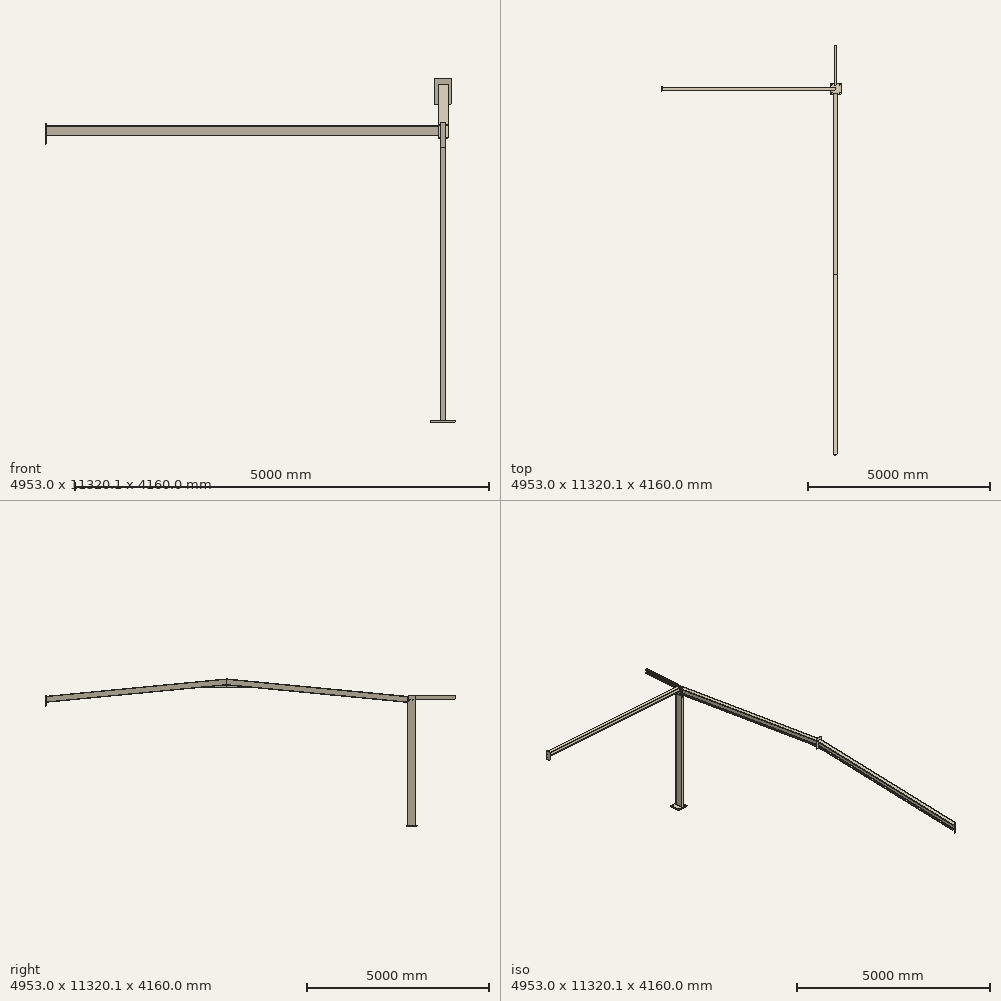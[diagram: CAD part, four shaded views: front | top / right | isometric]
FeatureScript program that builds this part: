
annotation { "Feature Type Name" : "Feature", "Feature Type Description" : "" }
export const myFeature = defineFeature(function(context is Context, id is Id, definition is map)
    precondition{}
    {
        {
            var Q0;
            Q0=qCreatedBy(makeId("Right.planeOp"),FACE);
            var sketch = newSketch(context, id + "F0", { "sketchPlane" : qUnion([Q0])});
            skLineSegment(sketch, "E0", {"start": v(-363, 0) * mm, "end": v(480.55, 0) * mm, "construction": true});
            skLineSegment(sketch, "E1", {"start": v(0, 0) * mm, "end": v(-4976.98, -479.23) * mm, "construction": true});
            skLineSegment(sketch, "E2", {"start": v(0, 0) * mm, "end": v(-23.08, 239.68) * mm, "construction": true});
            skLineSegment(sketch, "E3", {"start": v(0, 0) * mm, "end": v(4976.98, -479.23) * mm, "construction": true});
            skLineSegment(sketch, "E4", {"start": v(0, 0) * mm, "end": v(23.08, 239.68) * mm, "construction": true});
            skLineSegment(sketch, "E5.0", {"start": v(4976.98, -479.23) * mm, "end": v(5000.06, -239.54) * mm});
            skLineSegment(sketch, "E6.0", {"start": v(-4976.98, -479.23) * mm, "end": v(-5000.06, -239.54) * mm});
            skPoint(sketch, "E7.orphan", {"position": v(480.55, -46.27) * mm});
            skSolve(sketch);
        }
        {
            var Q0;
            Q0=sQuery(id+"F0.wireOp",EDGE,"E2");
            cPlane(context, id + "F1", {"entities" : qUnion([Q0]), "cplaneType" : CPlaneType.LINE_ANGLE, "offset" : 25 * mm, "angle" : 90 * degree, "width" : 150 * mm, "height" : 150 * mm});
        }
        {
            var Q0;
            Q0=sQuery(id+"F0.wireOp",EDGE,"E4");
            cPlane(context, id + "F2", {"entities" : qUnion([Q0]), "cplaneType" : CPlaneType.LINE_ANGLE, "offset" : 25 * mm, "angle" : 90 * degree, "width" : 150 * mm, "height" : 150 * mm});
        }
        {
            var Q0;
            Q0=qCreatedBy(makeId("Front.planeOp"),FACE);
            var sketch = newSketch(context, id + "F3", { "sketchPlane" : qUnion([Q0])});
            skLineSegment(sketch, "E8.bottom", {"start": v(100, -160) * mm, "end": v(-100, -160) * mm});
            skLineSegment(sketch, "E8.top", {"start": v(100, 160) * mm, "end": v(-100, 160) * mm});
            skLineSegment(sketch, "E8.left", {"start": v(100, -160) * mm, "end": v(100, 160) * mm});
            skLineSegment(sketch, "E8.right", {"start": v(-100, -160) * mm, "end": v(-100, 160) * mm});
            skPoint(sketch, "E8.middle", {"position": v(0, 0) * mm});
            skSolve(sketch);
        }
        {
            var Q0;
            Q0=qCreatedBy(id+"F1.planeOp",FACE);
            cPlane(context, id + "F4", {"entities" : qUnion([Q0]), "cplaneType" : CPlaneType.OFFSET, "offset" : 5000 * mm, "oppositeDirection" : true, "width" : 150 * mm, "height" : 150 * mm});
        }
        {
            var Q0;
            Q0=qCreatedBy(id+"F2.planeOp",FACE);
            cPlane(context, id + "F5", {"entities" : qUnion([Q0]), "cplaneType" : CPlaneType.OFFSET, "offset" : 5020 * mm, "width" : 150 * mm, "height" : 150 * mm});
        }
        {
            var Q0;
            Q0=qCreatedBy(id+"F5.planeOp",FACE);
            var sketch = newSketch(context, id + "F6", { "sketchPlane" : qUnion([Q0])});
            skLineSegment(sketch, "E9", {"start": v(60, 82.46) * mm, "end": v(-60, 82.46) * mm});
            skLineSegment(sketch, "E10", {"start": v(-60, 82.46) * mm, "end": v(-60, 72.46) * mm});
            skLineSegment(sketch, "E11", {"start": v(-60, 72.46) * mm, "end": v(-5, 72.46) * mm});
            skLineSegment(sketch, "E12", {"start": v(-5, 72.46) * mm, "end": v(-5, -72.46) * mm});
            skLineSegment(sketch, "E13", {"start": v(-5, -72.46) * mm, "end": v(-60, -72.46) * mm});
            skLineSegment(sketch, "E14", {"start": v(-60, -72.46) * mm, "end": v(-60, -82.46) * mm});
            skLineSegment(sketch, "E15", {"start": v(-60, -82.46) * mm, "end": v(60, -82.46) * mm});
            skLineSegment(sketch, "E16", {"start": v(60, -82.46) * mm, "end": v(60, -72.46) * mm});
            skLineSegment(sketch, "E17", {"start": v(60, -72.46) * mm, "end": v(5, -72.46) * mm});
            skLineSegment(sketch, "E18", {"start": v(5, -72.46) * mm, "end": v(5, 72.46) * mm});
            skLineSegment(sketch, "E19", {"start": v(5, 72.46) * mm, "end": v(60, 72.46) * mm});
            skLineSegment(sketch, "E20", {"start": v(60, 72.46) * mm, "end": v(60, 82.46) * mm});
            skPoint(sketch, "E21", {"position": v(-322.82, 17) * mm});
            skLineSegment(sketch, "E22", {"start": v(-5, 0) * mm, "end": v(5, 0) * mm, "construction": true});
            skPoint(sketch, "E23", {"position": v(0, 0) * mm});
            skSolve(sketch);
        }
        {
            var Q0;
            Q0=qSketchRegion(id+"F3",true);
            extrude(context, id + "F7", {"entities" : qUnion([Q0]), "depth" : 10 * mm});
        }
        {
            var Q0;
            Q0=qSketchRegion(id+"F6",true);
            extrude(context, id + "F8", {"entities" : qUnion([Q0]), "operationType" : NewBodyOperationType.ADD, "endBound" : BoundingType.UP_TO_NEXT, "oppositeDirection" : true, "depth" : 25 * mm});
        }
        {
            var Q0;
            Q0=qCreatedBy(id+"F4.planeOp",FACE);
            var sketch = newSketch(context, id + "F9", { "sketchPlane" : qUnion([Q0])});
            skLineSegment(sketch, "E24", {"start": v(60, 82.46) * mm, "end": v(-60, 82.46) * mm});
            skLineSegment(sketch, "E25", {"start": v(-60, 82.46) * mm, "end": v(-60, 72.46) * mm});
            skLineSegment(sketch, "E26", {"start": v(-60, 72.46) * mm, "end": v(-5, 72.46) * mm});
            skLineSegment(sketch, "E27", {"start": v(-5, 72.46) * mm, "end": v(-5, -72.46) * mm});
            skLineSegment(sketch, "E28", {"start": v(-5, -72.46) * mm, "end": v(-60, -72.46) * mm});
            skLineSegment(sketch, "E29", {"start": v(-60, -72.46) * mm, "end": v(-60, -82.46) * mm});
            skLineSegment(sketch, "E30", {"start": v(-60, -82.46) * mm, "end": v(60, -82.46) * mm});
            skLineSegment(sketch, "E31", {"start": v(60, -82.46) * mm, "end": v(60, -72.46) * mm});
            skLineSegment(sketch, "E32", {"start": v(60, -72.46) * mm, "end": v(5, -72.46) * mm});
            skLineSegment(sketch, "E33", {"start": v(5, -72.46) * mm, "end": v(5, 72.46) * mm});
            skLineSegment(sketch, "E34", {"start": v(5, 72.46) * mm, "end": v(60, 72.46) * mm});
            skLineSegment(sketch, "E35", {"start": v(60, 72.46) * mm, "end": v(60, 82.46) * mm});
            skPoint(sketch, "E36", {"position": v(-971.4, 551) * mm});
            skLineSegment(sketch, "E37", {"start": v(-5, 0) * mm, "end": v(5, 0) * mm, "construction": true});
            skPoint(sketch, "E38", {"position": v(0, 0) * mm});
            skSolve(sketch);
        }
        {
            var Q0;
            Q0=qSketchRegion(id+"F9",true);
            extrude(context, id + "F10", {"entities" : qUnion([Q0]), "operationType" : NewBodyOperationType.ADD, "endBound" : BoundingType.UP_TO_NEXT, "depth" : 25 * mm});
        }
        {
            var Q0;
            Q0=qCreatedBy(makeId("Top.planeOp"),FACE);
            cPlane(context, id + "F11", {"entities" : qUnion([Q0]), "cplaneType" : CPlaneType.OFFSET, "offset" : 4000 * mm, "oppositeDirection" : true, "width" : 150 * mm, "height" : 150 * mm});
        }
        {
            var Q0;
            Q0=qCreatedBy(id+"F11.planeOp",FACE);
            var sketch = newSketch(context, id + "F12", { "sketchPlane" : qUnion([Q0])});
            skLineSegment(sketch, "E39.bottom", {"start": v(150, 5276.98) * mm, "end": v(-150, 5276.98) * mm});
            skLineSegment(sketch, "E39.top", {"start": v(150, 4976.98) * mm, "end": v(-150, 4976.98) * mm});
            skLineSegment(sketch, "E39.left", {"start": v(150, 5276.98) * mm, "end": v(150, 4976.98) * mm});
            skLineSegment(sketch, "E39.right", {"start": v(-150, 5276.98) * mm, "end": v(-150, 4976.98) * mm});
            skLineSegment(sketch, "E40", {"start": v(150, 4976.98) * mm, "end": v(-150, 5276.98) * mm, "construction": true});
            skPoint(sketch, "E41", {"position": v(0, 4976.98) * mm});
            skSolve(sketch);
        }
        {
            var Q0;
            Q0=qSketchRegion(id+"F12",true);
            extrude(context, id + "F13", {"entities" : qUnion([Q0]), "depth" : 25 * mm});
        }
        {
            var Q0;
            Q0=makeQuery(id+"F13.opExtrude","CAP_FACE",FACE,{"disambiguationData":[OSD([sQuery(id+"F12.wireOp",EDGE,"E39.bottom"),sQuery(id+"F12.wireOp",EDGE,"E39.top"),sQuery(id+"F12.wireOp",EDGE,"E39.left"),sQuery(id+"F12.wireOp",EDGE,"E39.right")])],"isStart":false});
            var sketch = newSketch(context, id + "F14", { "sketchPlane" : qUnion([Q0])});
            skLineSegment(sketch, "E42", {"start": v(25.6, 5220.06) * mm, "end": v(-25.6, 5220.06) * mm});
            skLineSegment(sketch, "E43", {"start": v(-25.6, 5220.06) * mm, "end": v(-25.6, 5212.06) * mm});
            skLineSegment(sketch, "E44", {"start": v(-25.6, 5212.06) * mm, "end": v(-3, 5212.06) * mm});
            skLineSegment(sketch, "E45", {"start": v(-3, 5212.06) * mm, "end": v(-3, 5008.06) * mm});
            skLineSegment(sketch, "E46", {"start": v(-3, 5008.06) * mm, "end": v(-25.6, 5008.06) * mm});
            skLineSegment(sketch, "E47", {"start": v(-25.6, 5008.06) * mm, "end": v(-25.6, 5000.06) * mm});
            skLineSegment(sketch, "E48", {"start": v(-25.6, 5000.06) * mm, "end": v(25.6, 5000.06) * mm});
            skLineSegment(sketch, "E49", {"start": v(25.6, 5000.06) * mm, "end": v(25.6, 5008.06) * mm});
            skPoint(sketch, "E49.endSnap0", {"position": v(-14.3, 5008.06) * mm});
            skLineSegment(sketch, "E50", {"start": v(25.6, 5008.06) * mm, "end": v(3, 5008.06) * mm});
            skLineSegment(sketch, "E51", {"start": v(3, 5008.06) * mm, "end": v(3, 5212.06) * mm});
            skLineSegment(sketch, "E52", {"start": v(3, 5212.06) * mm, "end": v(25.6, 5212.06) * mm});
            skLineSegment(sketch, "E53", {"start": v(25.6, 5212.06) * mm, "end": v(25.6, 5220.06) * mm});
            skPoint(sketch, "E54", {"position": v(0, 5000.06) * mm});
            skSolve(sketch);
        }
        {
            var Q0;
            Q0=qSketchRegion(id+"F14",true);
            extrude(context, id + "F15", {"entities" : qUnion([Q0]), "operationType" : NewBodyOperationType.ADD, "depth" : 3600 * mm});
        }
        {
            var Q0;
            Q0=makeQuery(id+"F15.opExtrude","SWEPT_FACE",FACE,{"disambiguationData":[OSD([sQuery(id+"F14.wireOp",EDGE,"E42")])]});
            var sketch = newSketch(context, id + "F16", { "sketchPlane" : qUnion([Q0])});
            skLineSegment(sketch, "E55", {"start": v(25, -379.23) * mm, "end": v(-25, -379.23) * mm});
            skLineSegment(sketch, "E56", {"start": v(-25, -379.23) * mm, "end": v(-25, -479.23) * mm});
            skLineSegment(sketch, "E57", {"start": v(-25, -479.23) * mm, "end": v(25, -479.23) * mm});
            skLineSegment(sketch, "E58", {"start": v(25, -479.23) * mm, "end": v(25, -469.23) * mm});
            skLineSegment(sketch, "E59", {"start": v(25, -469.23) * mm, "end": v(-19, -469.23) * mm});
            skLineSegment(sketch, "E60", {"start": v(-19, -469.23) * mm, "end": v(-19, -389.23) * mm});
            skLineSegment(sketch, "E61", {"start": v(-19, -389.23) * mm, "end": v(25, -389.23) * mm});
            skLineSegment(sketch, "E62", {"start": v(25, -389.23) * mm, "end": v(25, -379.23) * mm});
            skPoint(sketch, "E63", {"position": v(0, -479.23) * mm});
            skSolve(sketch);
        }
        {
            var Q0;
            Q0=qSketchRegion(id+"F16",true);
            extrude(context, id + "F17", {"entities" : qUnion([Q0]), "operationType" : NewBodyOperationType.ADD, "depth" : 1100 * mm});
        }
        {
            var Q0;
            Q0=makeQuery(id+"F15.opExtrude","SWEPT_FACE",FACE,{"disambiguationData":[OSD([sQuery(id+"F14.wireOp",EDGE,"E45")])]});
            var sketch = newSketch(context, id + "F18", { "sketchPlane" : qUnion([Q0])});
            skLineSegment(sketch, "E64.bottom", {"start": v(-5175.06, -385) * mm, "end": v(-5045.06, -385) * mm});
            skLineSegment(sketch, "E64.top", {"start": v(-5175.06, -635) * mm, "end": v(-5045.06, -635) * mm});
            skLineSegment(sketch, "E64.left", {"start": v(-5175.06, -385) * mm, "end": v(-5175.06, -635) * mm});
            skLineSegment(sketch, "E64.right", {"start": v(-5045.06, -385) * mm, "end": v(-5045.06, -635) * mm});
            skPoint(sketch, "E65", {"position": v(-5110.06, -385) * mm});
            skSolve(sketch);
        }
        {
            var Q0;
            Q0=makeQuery(id+"F15.opExtrude","SWEPT_FACE",FACE,{"disambiguationData":[OSD([sQuery(id+"F14.wireOp",EDGE,"E45")])]});
            var sketch = newSketch(context, id + "F19", { "sketchPlane" : qUnion([Q0])});
            skLineSegment(sketch, "E66", {"start": v(-5153.56, -414) * mm, "end": v(-5066.56, -414) * mm});
            skLineSegment(sketch, "E67", {"start": v(-5066.56, -414) * mm, "end": v(-5066.56, -420) * mm});
            skLineSegment(sketch, "E68", {"start": v(-5066.56, -420) * mm, "end": v(-5107.06, -420) * mm});
            skLineSegment(sketch, "E69", {"start": v(-5107.06, -420) * mm, "end": v(-5107.06, -529) * mm});
            skLineSegment(sketch, "E70", {"start": v(-5107.06, -529) * mm, "end": v(-5066.56, -529) * mm});
            skLineSegment(sketch, "E71", {"start": v(-5066.56, -529) * mm, "end": v(-5066.56, -535) * mm});
            skLineSegment(sketch, "E72", {"start": v(-5066.56, -535) * mm, "end": v(-5153.56, -535) * mm});
            skLineSegment(sketch, "E73", {"start": v(-5153.56, -535) * mm, "end": v(-5153.56, -529) * mm});
            skLineSegment(sketch, "E74", {"start": v(-5153.56, -529) * mm, "end": v(-5113.06, -529) * mm});
            skLineSegment(sketch, "E75", {"start": v(-5113.06, -529) * mm, "end": v(-5113.06, -420) * mm});
            skLineSegment(sketch, "E76", {"start": v(-5113.06, -420) * mm, "end": v(-5153.56, -420) * mm});
            skLineSegment(sketch, "E77", {"start": v(-5153.56, -420) * mm, "end": v(-5153.56, -414) * mm});
            skPoint(sketch, "E78", {"position": v(-5110.06, -535) * mm});
            skSolve(sketch);
        }
        {
            var Q0;
            Q0=qSketchRegion(id+"F19",true);
            extrude(context, id + "F20", {"entities" : qUnion([Q0]), "operationType" : NewBodyOperationType.ADD, "depth" : 4800 * mm});
        }
        {
            var Q0;
            Q0=qSketchRegion(id+"F18",true);
            extrude(context, id + "F21", {"entities" : qUnion([Q0]), "depth" : 10 * mm});
        }
        {
            var Q0;
            Q0=makeQuery(id+"F15.opExtrude","SWEPT_FACE",FACE,{"disambiguationData":[OSD([sQuery(id+"F14.wireOp",EDGE,"E48")])]});
            var sketch = newSketch(context, id + "F22", { "sketchPlane" : qUnion([Q0])});
            skLineSegment(sketch, "E79.bottom", {"start": v(-82.33, -365) * mm, "end": v(87.67, -365) * mm});
            skLineSegment(sketch, "E79.top", {"start": v(-82.33, -568.21) * mm, "end": v(87.67, -568.21) * mm});
            skLineSegment(sketch, "E79.left", {"start": v(-82.33, -365) * mm, "end": v(-82.33, -568.21) * mm});
            skLineSegment(sketch, "E79.right", {"start": v(87.67, -365) * mm, "end": v(87.67, -568.21) * mm});
            skSolve(sketch);
        }
        {
            var Q0;
            Q0 = qSketchRegion(id + "F22", true);
            extrude(context, id + "F23", {"entities" : qUnion([Q0]), "depth" : 15 * mm, "hasSecondDirection" : true, "secondDirectionOppositeDirection" : true, "secondDirectionDepth" : 25 * mm});
        }
        {
            var Q0;
            Q0=makeQuery(id+"F23.opExtrude","SWEPT_BODY",BODY,{"disambiguationData":[OSD([sQuery(id+"F22.wireOp",EDGE,"E79.bottom"),sQuery(id+"F22.wireOp",EDGE,"E79.top"),sQuery(id+"F22.wireOp",EDGE,"E79.left"),sQuery(id+"F22.wireOp",EDGE,"E79.right")])]});
            var Q1;
            Q1=makeQuery(id+"F7.opExtrude","SWEPT_BODY",BODY,{"disambiguationData":[OSD([sQuery(id+"F3.wireOp",EDGE,"E8.bottom"),sQuery(id+"F3.wireOp",EDGE,"E8.top"),sQuery(id+"F3.wireOp",EDGE,"E8.left"),sQuery(id+"F3.wireOp",EDGE,"E8.right")])]});
            booleanBodies(context, id + "F24", {"operationType" : BooleanOperationType.SUBTRACTION, "tools" : qUnion([Q0]), "targets" : qUnion([Q1])});
        }
        {
            var Q0;
            Q0=makeQuery(id+"F15.opExtrude","SWEPT_FACE",FACE,{"disambiguationData":[OSD([sQuery(id+"F14.wireOp",EDGE,"E48")])]});
            var sketch = newSketch(context, id + "F25", { "sketchPlane" : qUnion([Q0])});
            skLineSegment(sketch, "E80.bottom", {"start": v(-25.6, -375) * mm, "end": v(25.6, -375) * mm});
            skLineSegment(sketch, "E80.top", {"start": v(-25.6, -675) * mm, "end": v(25.6, -675) * mm});
            skLineSegment(sketch, "E80.left", {"start": v(-25.6, -375) * mm, "end": v(-25.6, -675) * mm});
            skLineSegment(sketch, "E80.right", {"start": v(25.6, -375) * mm, "end": v(25.6, -675) * mm});
            skSolve(sketch);
        }
        {
            var Q0;
            Q0 = qSketchRegion(id + "F25", true);
            extrude(context, id + "F26", {"entities" : qUnion([Q0]), "depth" : 15 * mm});
        }
        {
            var Q0;
            Q0=makeQuery(id+"F13.opExtrude","SWEPT_BODY",BODY,{"disambiguationData":[OSD([sQuery(id+"F12.wireOp",EDGE,"E39.bottom"),sQuery(id+"F12.wireOp",EDGE,"E39.top"),sQuery(id+"F12.wireOp",EDGE,"E39.left"),sQuery(id+"F12.wireOp",EDGE,"E39.right")])]});
            var Q1;
            Q1=makeQuery(id+"F26.opExtrude","SWEPT_BODY",BODY,{"disambiguationData":[OSD([sQuery(id+"F25.wireOp",EDGE,"E80.bottom"),sQuery(id+"F25.wireOp",EDGE,"E80.top"),sQuery(id+"F25.wireOp",EDGE,"E80.left"),sQuery(id+"F25.wireOp",EDGE,"E80.right")])]});
            var Q2;
            Q2=qCreatedBy(makeId("Front.planeOp"),FACE);
            mirror(context, id + "F27", {"entities" : qUnion([Q0, Q1]), "mirrorPlane" : qUnion([Q2])});
        }
        {
            var Q0;
            Q0=makeQuery(id+"F20.opExtrude","CAP_FACE",FACE,{"disambiguationData":[OSD([sQuery(id+"F19.wireOp",EDGE,"E66"),sQuery(id+"F19.wireOp",EDGE,"E67"),sQuery(id+"F19.wireOp",EDGE,"E68"),sQuery(id+"F19.wireOp",EDGE,"E69"),sQuery(id+"F19.wireOp",EDGE,"E70"),sQuery(id+"F19.wireOp",EDGE,"E71"),sQuery(id+"F19.wireOp",EDGE,"E72"),sQuery(id+"F19.wireOp",EDGE,"E73"),sQuery(id+"F19.wireOp",EDGE,"E74"),sQuery(id+"F19.wireOp",EDGE,"E75"),sQuery(id+"F19.wireOp",EDGE,"E76"),sQuery(id+"F19.wireOp",EDGE,"E77")])],"isStart":false});
            var sketch = newSketch(context, id + "F28", { "sketchPlane" : qUnion([Q0])});
            skCircle(sketch, "E81", {"center": v(-5153.06, -399.15) * mm, "radius": 9 * mm});
            skLineSegment(sketch, "E82", {"start": v(-5110.06, -414) * mm, "end": v(-5110.06, -359.35) * mm, "construction": true});
            skPoint(sketch, "E82.endSnap0", {"position": v(-5110.06, -414) * mm});
            skCircle(sketch, "E83.MirrorC", {"center": v(-5067.06, -399.15) * mm, "radius": 9 * mm});
            skCircle(sketch, "E84.0.1.0", {"center": v(-5067.54, -499.15) * mm, "radius": 9 * mm});
            skCircle(sketch, "E84.0.1.1", {"center": v(-5153.54, -499.15) * mm, "radius": 9 * mm});
            skCircle(sketch, "E84.0.2.0", {"center": v(-5068.02, -599.15) * mm, "radius": 9 * mm});
            skCircle(sketch, "E84.0.2.1", {"center": v(-5154.02, -599.15) * mm, "radius": 9 * mm});
            skLineSegment(sketch, "E84.direction1", {"start": v(-5067.06, -399.15) * mm, "end": v(-5039.06, -399.15) * mm, "construction": true});
            skLineSegment(sketch, "E84.direction2", {"start": v(-5067.06, -399.15) * mm, "end": v(-5067.54, -499.15) * mm, "construction": true});
            skSolve(sketch);
        }
        {
            var Q0;
            Q0 = qSketchRegion(id + "F28", true);
            extrude(context, id + "F29", {"entities" : qUnion([Q0]), "operationType" : NewBodyOperationType.REMOVE, "endBound" : BoundingType.THROUGH_ALL, "oppositeDirection" : true, "depth" : 25 * mm});
        }
        {
            var Q0;
            Q0=makeQuery(id+"F13.opExtrude","CAP_FACE",FACE,{"disambiguationData":[OSD([sQuery(id+"F12.wireOp",EDGE,"E39.bottom"),sQuery(id+"F12.wireOp",EDGE,"E39.top"),sQuery(id+"F12.wireOp",EDGE,"E39.left"),sQuery(id+"F12.wireOp",EDGE,"E39.right")])],"isStart":false});
            var sketch = newSketch(context, id + "F30", { "sketchPlane" : qUnion([Q0])});
            skCircle(sketch, "E85", {"center": v(110, 5236.98) * mm, "radius": 12 * mm});
            skLineSegment(sketch, "E86", {"start": v(150, 5126.98) * mm, "end": v(192.32, 5126.98) * mm, "construction": true});
            skLineSegment(sketch, "E87", {"start": v(0, 5276.98) * mm, "end": v(0, 5382.82) * mm, "construction": true});
            skCircle(sketch, "E88.MirrorC", {"center": v(110, 5016.98) * mm, "radius": 12 * mm});
            skCircle(sketch, "E89.MirrorC", {"center": v(-110, 5236.98) * mm, "radius": 12 * mm});
            skCircle(sketch, "E90.MirrorC", {"center": v(-110, 5016.98) * mm, "radius": 12 * mm});
            skSolve(sketch);
        }
        {
            var Q0;
            Q0 = qSketchRegion(id + "F30", true);
            extrude(context, id + "F31", {"entities" : qUnion([Q0]), "operationType" : NewBodyOperationType.REMOVE, "oppositeDirection" : true, "depth" : 40 * mm});
        }
        {
            var Q0;
            Q0=makeQuery(id+"F20.opExtrude","SWEPT_FACE",FACE,{"disambiguationData":[OSD([sQuery(id+"F19.wireOp",EDGE,"E66")])]});
            var sketch = newSketch(context, id + "F32", { "sketchPlane" : qUnion([Q0])});
            skLineSegment(sketch, "E91", {"start": v(-2403, 5153.56) * mm, "end": v(-2403, 4659.05) * mm, "construction": true});
            skSolve(sketch);
        }
        {
            var Q0;
            Q0=sQuery(id+"F32.wireOp",EDGE,"E91");
            cPlane(context, id + "F33", {"entities" : qUnion([Q0]), "cplaneType" : CPlaneType.LINE_ANGLE, "offset" : 25 * mm, "angle" : 90 * degree, "width" : 150 * mm, "height" : 150 * mm});
        }
        {
            var Q0;
            Q0=makeQuery(id+"F21.opExtrude","SWEPT_BODY",BODY,{"disambiguationData":[OSD([sQuery(id+"F18.wireOp",EDGE,"E64.bottom"),sQuery(id+"F18.wireOp",EDGE,"E64.top"),sQuery(id+"F18.wireOp",EDGE,"E64.left"),sQuery(id+"F18.wireOp",EDGE,"E64.right")])]});
            var Q1;
            Q1=qCreatedBy(id+"F33.planeOp",FACE);
            mirror(context, id + "F34", {"operationType" : NewBodyOperationType.ADD, "entities" : qUnion([Q0]), "mirrorPlane" : qUnion([Q1])});
        }
        {
            var Q0;
            Q0=makeQuery(id+"F7.opExtrude","SWEPT_FACE",FACE,{"disambiguationData":[OSD([sQuery(id+"F3.wireOp",EDGE,"E8.top")])]});
            var sketch = newSketch(context, id + "F35", { "sketchPlane" : qUnion([Q0])});
            skLineSegment(sketch, "E92", {"start": v(0, 0) * mm, "end": v(0, -69.19) * mm, "construction": true});
            skPoint(sketch, "E92.endSnap0", {"position": v(0, -10) * mm});
            skSolve(sketch);
        }
        {
            var Q0;
            Q0=sQuery(id+"F35.wireOp",EDGE,"E92");
            cPlane(context, id + "F36", {"entities" : qUnion([Q0]), "cplaneType" : CPlaneType.LINE_ANGLE, "offset" : 25 * mm, "angle" : 90 * degree, "width" : 150 * mm, "height" : 150 * mm});
        }
        {
            var Q0;
            Q0=qCreatedBy(id+"F36.planeOp",FACE);
            var sketch = newSketch(context, id + "F37", { "sketchPlane" : qUnion([Q0])});
            skLineSegment(sketch, "E93", {"start": v(0, -154.79) * mm, "end": v(0, -82.84) * mm});
            skLineSegment(sketch, "E94", {"start": v(0, -82.84) * mm, "end": v(771.44, -154.79) * mm});
            skLineSegment(sketch, "E95", {"start": v(0, -154.79) * mm, "end": v(771.44, -154.79) * mm});
            skSolve(sketch);
        }
        {
            var Q0;
            Q0 = qSketchRegion(id + "F37", true);
            extrude(context, id + "F38", {"entities" : qUnion([Q0]), "depth" : 5 * mm, "hasSecondDirection" : true, "secondDirectionOppositeDirection" : true, "secondDirectionDepth" : 5 * mm});
        }
        {
            var Q0;
            Q0=makeQuery(id+"F38.opExtrude","SWEPT_BODY",BODY,{"disambiguationData":[OSD([sQuery(id+"F37.wireOp",EDGE,"E93"),sQuery(id+"F37.wireOp",EDGE,"E94"),sQuery(id+"F37.wireOp",EDGE,"E95")])]});
            var Q1;
            Q1=qCreatedBy(makeId("Front.planeOp"),FACE);
            mirror(context, id + "F39", {"entities" : qUnion([Q0]), "mirrorPlane" : qUnion([Q1])});
        }
    });
